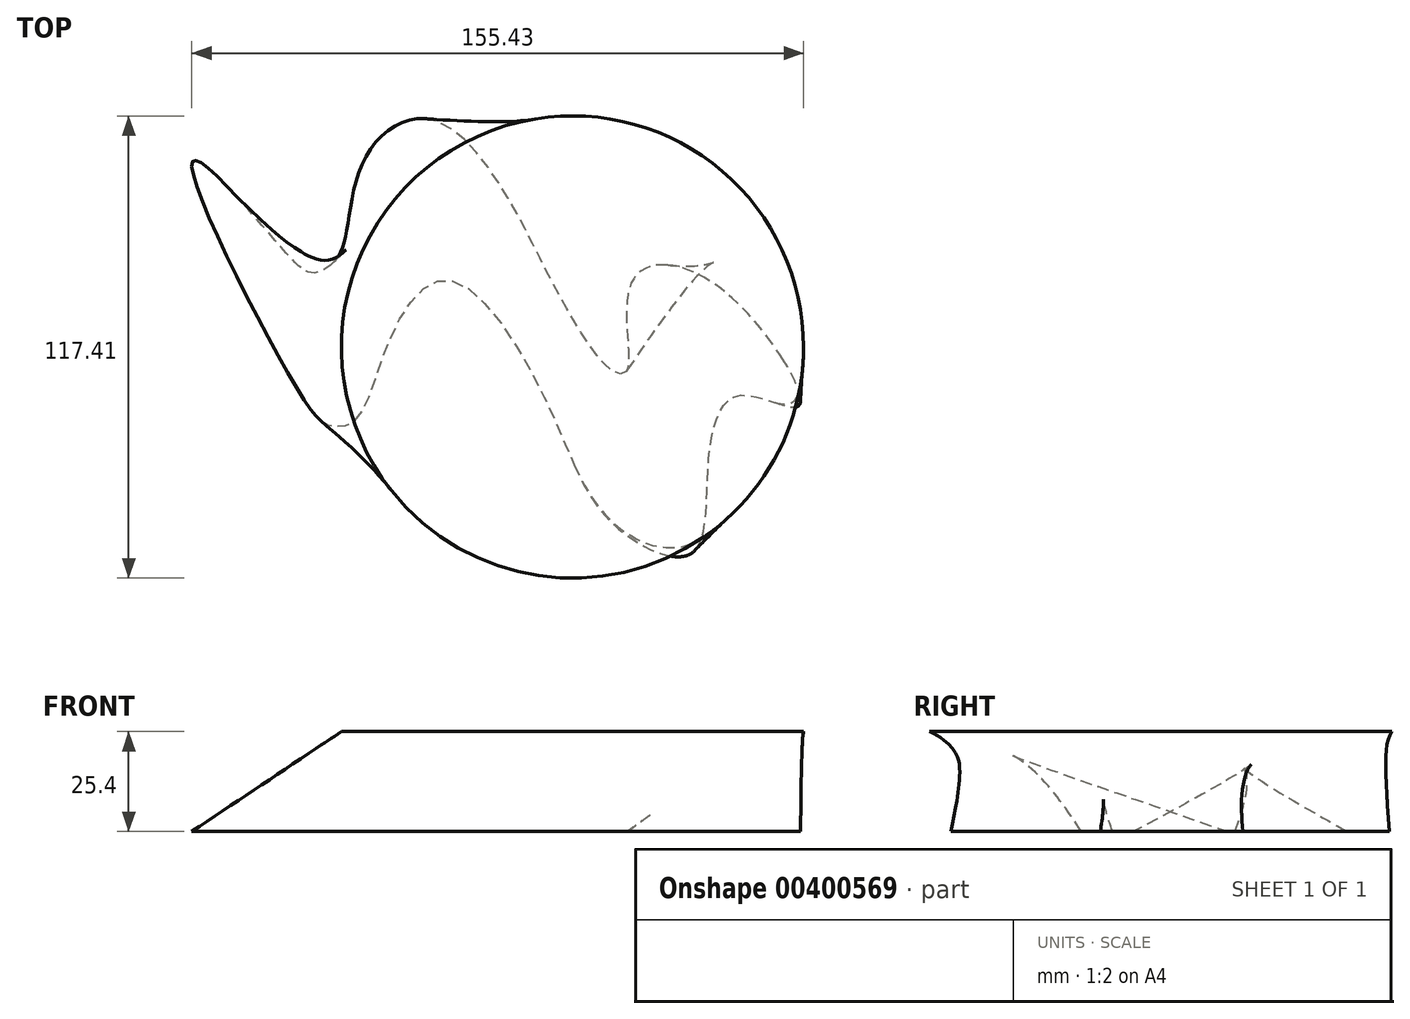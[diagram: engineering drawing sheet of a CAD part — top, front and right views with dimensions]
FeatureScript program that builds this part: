
annotation { "Feature Type Name" : "Feature", "Feature Type Description" : "" }
export const myFeature = defineFeature(function(context is Context, id is Id, definition is map)
    precondition{}
    {
        {
            var Q0;
            Q0=qCreatedBy(makeId("Top.planeOp"),FACE);
            cPlane(context, id + "F0", {"entities" : qUnion([Q0]), "cplaneType" : CPlaneType.OFFSET, "offset" : 25.4 * mm, "width" : 152.4 * mm, "height" : 152.4 * mm});
        }
        {
            var Q0;
            Q0=qCreatedBy(id+"F0.planeOp",FACE);
            var sketch = newSketch(context, id + "F1", { "sketchPlane" : qUnion([Q0])});
            skCircle(sketch, "E0", {"center": v(-10.08, 6.03) * mm, "radius": 58.7 * mm});
            skSolve(sketch);
        }
        {
            var Q0;
            Q0=qCreatedBy(makeId("Top.planeOp"),FACE);
            var sketch = newSketch(context, id + "F2", { "sketchPlane" : qUnion([Q0])});
            skFitSpline(sketch, "E1", {"points": [v(-106.57, 53.22) * mm, v(-77.82, -8) * mm, v(-71.06, -13.99) * mm, v(-65.26, -12.62) * mm, v(-56.29, 8.4) * mm, v(-41.3, 22.98) * mm, v(-15.79, -9.78) * mm, v(0, -38.68) * mm, v(19.94, -46.53) * mm, v(24.44, -23.48) * mm, v(32.62, -6.23) * mm, v(47.36, -8.93) * mm, v(26.86, 21.44) * mm, v(5.04, 22.7) * mm, v(3.7, 0) * mm, v(0, 0) * mm, v(-8.87, 11.37) * mm, v(-17.2, 26.35) * mm, v(-29.26, 48.4) * mm, v(-46.83, 63.97) * mm, v(-62.16, 55.12) * mm, v(-67.6, 34.84) * mm, v(-70.5, 27.88) * mm, v(-75.7, 24.88) * mm, v(-84.02, 31.3) * mm, v(-106.57, 53.22) * mm]});
            skSolve(sketch);
        }
        {
            var Q0;
            Q0 = qSketchRegion(id + "F1", true);
            var Q1;
            Q1 = qSketchRegion(id + "F2", true);
            loft(context, id + "F3", {"sheetProfilesArray" : [{ "sheetProfileEntities" : qUnion([Q0]) }, { "sheetProfileEntities" : qUnion([Q1]) }]});
        }
    });
